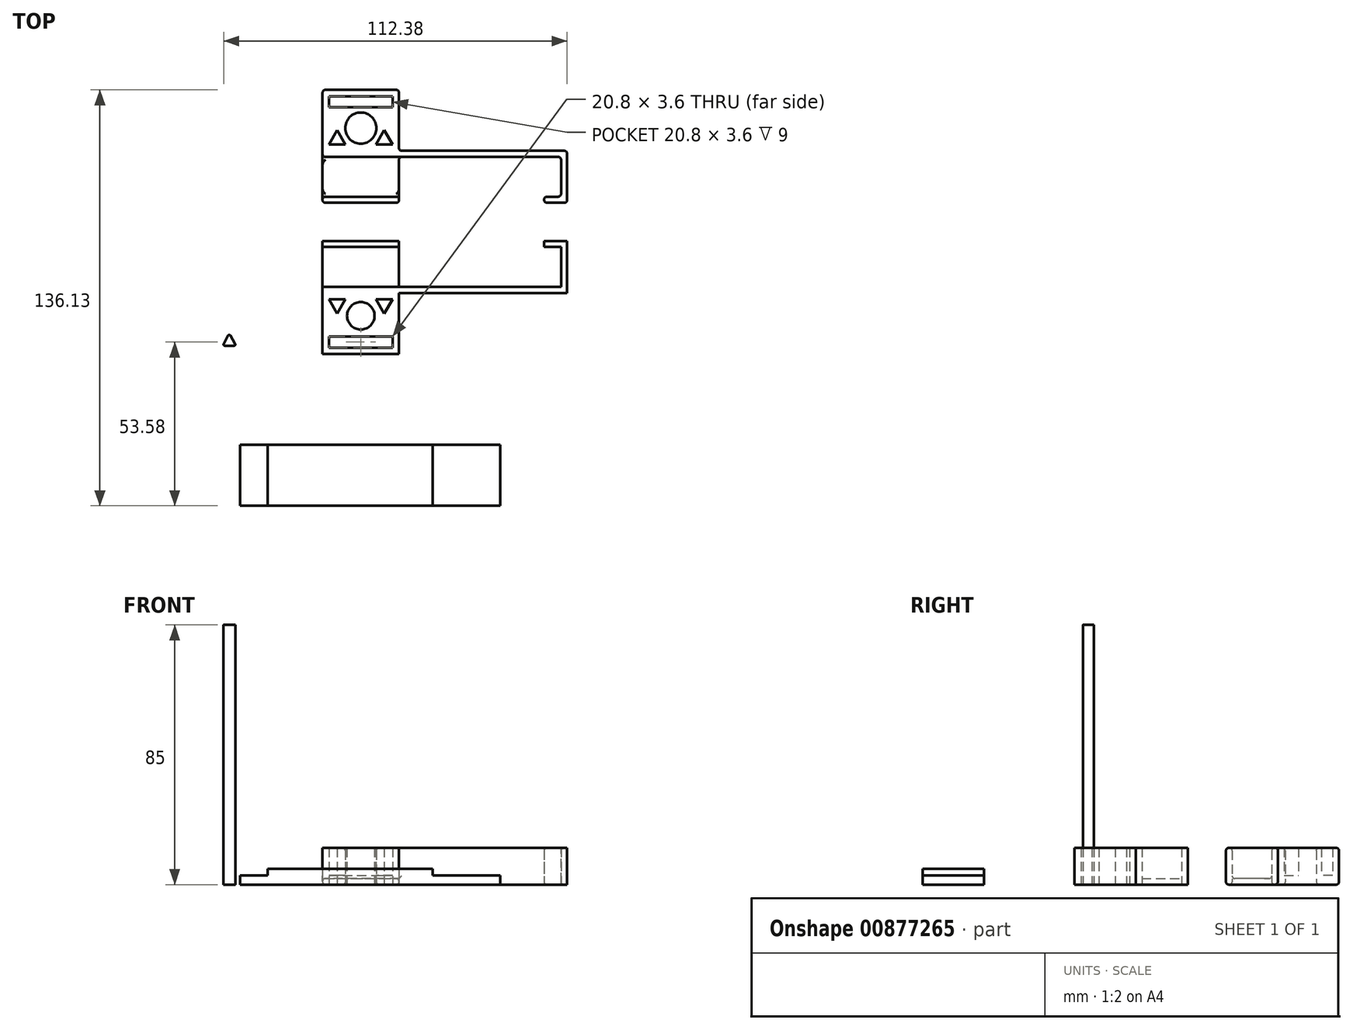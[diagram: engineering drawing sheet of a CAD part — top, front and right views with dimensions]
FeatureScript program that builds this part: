
annotation { "Feature Type Name" : "Feature", "Feature Type Description" : "" }
export const myFeature = defineFeature(function(context is Context, id is Id, definition is map)
    precondition{}
    {
        {
            var Q0;
            Q0=qCreatedBy(makeId("Top.planeOp"),FACE);
            var sketch = newSketch(context, id + "F0", { "sketchPlane" : qUnion([Q0])});
            skLineSegment(sketch, "E0.bottom", {"start": v(0, 0) * mm, "end": v(55, 0) * mm});
            skLineSegment(sketch, "E0.left", {"start": v(-25, 0) * mm, "end": v(-25, 2) * mm});
            skLineSegment(sketch, "E0.right", {"start": v(55, 0) * mm, "end": v(55, 2) * mm});
            skLineSegment(sketch, "E1.top", {"start": v(55, 17) * mm, "end": v(53, 17) * mm});
            skLineSegment(sketch, "E1.left", {"start": v(55, 2) * mm, "end": v(55, 17) * mm});
            skLineSegment(sketch, "E1.right", {"start": v(53, 2) * mm, "end": v(53, 15) * mm});
            skLineSegment(sketch, "E2.bottom", {"start": v(53, 17) * mm, "end": v(47.5, 17) * mm});
            skLineSegment(sketch, "E2.top", {"start": v(53, 15) * mm, "end": v(47.5, 15) * mm});
            skLineSegment(sketch, "E2.right", {"start": v(47.5, 17) * mm, "end": v(47.5, 15) * mm});
            skLineSegment(sketch, "E3", {"start": v(0, 2) * mm, "end": v(53, 2) * mm});
            skLineSegment(sketch, "E4.top", {"start": v(-25, -20) * mm, "end": v(0, -20) * mm});
            skLineSegment(sketch, "E4.left", {"start": v(-25, 0) * mm, "end": v(-25, -20) * mm});
            skLineSegment(sketch, "E4.right", {"start": v(0, 0) * mm, "end": v(0, -20) * mm});
            skLineSegment(sketch, "E5.top", {"start": v(-25, 17) * mm, "end": v(0, 17) * mm});
            skLineSegment(sketch, "E5.left", {"start": v(-25, 2) * mm, "end": v(-25, 17) * mm});
            skLineSegment(sketch, "E5.right", {"start": v(0, 2) * mm, "end": v(0, 17) * mm});
            skPoint(sketch, "E6", {"position": v(-12.5, -7.5) * mm});
            skCircle(sketch, "E7", {"center": v(-12.5, -7.5) * mm, "radius": 4.5 * mm});
            skLineSegment(sketch, "E8.bottom", {"start": v(0, 46.45) * mm, "end": v(-25, 46.45) * mm});
            skLineSegment(sketch, "E8.top", {"start": v(0, 66.45) * mm, "end": v(-25, 66.45) * mm});
            skLineSegment(sketch, "E8.left", {"start": v(0, 46.45) * mm, "end": v(0, 66.45) * mm});
            skLineSegment(sketch, "E8.right", {"start": v(-25, 46.45) * mm, "end": v(-25, 66.45) * mm});
            skLineSegment(sketch, "E9.bottom", {"start": v(0, 44.5) * mm, "end": v(-25, 44.5) * mm});
            skLineSegment(sketch, "E9.top", {"start": v(0, 29.5) * mm, "end": v(-25, 29.5) * mm});
            skLineSegment(sketch, "E9.left", {"start": v(0, 44.5) * mm, "end": v(0, 29.5) * mm});
            skLineSegment(sketch, "E9.right", {"start": v(-25, 44.5) * mm, "end": v(-25, 29.5) * mm});
            skPoint(sketch, "E10", {"position": v(-12.5, 53.95) * mm});
            skCircle(sketch, "E11", {"center": v(-12.5, 53.95) * mm, "radius": 5.1 * mm});
            skLineSegment(sketch, "E12", {"start": v(-25, 46.45) * mm, "end": v(-25, 44.5) * mm});
            skLineSegment(sketch, "E13", {"start": v(0, 46.5) * mm, "end": v(55, 46.5) * mm});
            skLineSegment(sketch, "E14", {"start": v(55, 46.5) * mm, "end": v(55, 29.5) * mm});
            skLineSegment(sketch, "E15", {"start": v(0, 44.5) * mm, "end": v(53, 44.5) * mm});
            skLineSegment(sketch, "E16", {"start": v(55, 29.5) * mm, "end": v(47.5, 29.5) * mm});
            skLineSegment(sketch, "E17", {"start": v(47.5, 29.5) * mm, "end": v(47.5, 31.5) * mm});
            skLineSegment(sketch, "E18", {"start": v(47.5, 31.5) * mm, "end": v(53, 31.5) * mm});
            skLineSegment(sketch, "E19", {"start": v(53, 31.5) * mm, "end": v(53, 44.5) * mm});
            skLineSegment(sketch, "E20", {"start": v(-25, 2) * mm, "end": v(0, 2) * mm});
            skLineSegment(sketch, "E21", {"start": v(0, 0) * mm, "end": v(-25, 0) * mm});
            skLineSegment(sketch, "E22", {"start": v(-20.2, 53.23) * mm, "end": v(-22.9, 48.55) * mm});
            skLineSegment(sketch, "E23", {"start": v(-22.9, 48.55) * mm, "end": v(-17.5, 48.55) * mm});
            skLineSegment(sketch, "E24", {"start": v(-17.5, 48.55) * mm, "end": v(-20.2, 53.23) * mm});
            skLineSegment(sketch, "E25", {"start": v(-12.5, 53.95) * mm, "end": v(-12.5, -32.35) * mm, "construction": true});
            skLineSegment(sketch, "E26.MirrorCS", {"start": v(-4.8, 53.23) * mm, "end": v(-2.1, 48.55) * mm});
            skLineSegment(sketch, "E27.MirrorCS", {"start": v(-7.5, 48.55) * mm, "end": v(-4.8, 53.23) * mm});
            skLineSegment(sketch, "E28.MirrorCS", {"start": v(-2.1, 48.55) * mm, "end": v(-7.5, 48.55) * mm});
            skLineSegment(sketch, "E29", {"start": v(-54.87, 23.25) * mm, "end": v(73.63, 23.25) * mm, "construction": true});
            skLineSegment(sketch, "E30.MirrorCS", {"start": v(-17.5, -2.05) * mm, "end": v(-20.2, -6.73) * mm});
            skLineSegment(sketch, "E31.MirrorCS", {"start": v(-20.2, -6.73) * mm, "end": v(-22.9, -2.05) * mm});
            skLineSegment(sketch, "E32.MirrorCS", {"start": v(-22.9, -2.05) * mm, "end": v(-17.5, -2.05) * mm});
            skLineSegment(sketch, "E33.MirrorCS", {"start": v(-2.1, -2.05) * mm, "end": v(-7.5, -2.05) * mm});
            skLineSegment(sketch, "E34.MirrorCS", {"start": v(-4.8, -6.73) * mm, "end": v(-2.1, -2.05) * mm});
            skLineSegment(sketch, "E35.MirrorCS", {"start": v(-7.5, -2.05) * mm, "end": v(-4.8, -6.73) * mm});
            skLineSegment(sketch, "E36.bottom", {"start": v(-22.9, -14.3) * mm, "end": v(-2.1, -14.3) * mm});
            skLineSegment(sketch, "E36.top", {"start": v(-22.9, -17.9) * mm, "end": v(-2.1, -17.9) * mm});
            skLineSegment(sketch, "E36.left", {"start": v(-22.9, -14.3) * mm, "end": v(-22.9, -17.9) * mm});
            skLineSegment(sketch, "E36.right", {"start": v(-2.1, -14.3) * mm, "end": v(-2.1, -17.9) * mm});
            skLineSegment(sketch, "E37.bottom", {"start": v(-22.9, 64.35) * mm, "end": v(-2.1, 64.35) * mm});
            skLineSegment(sketch, "E37.top", {"start": v(-22.9, 60.75) * mm, "end": v(-2.1, 60.75) * mm});
            skLineSegment(sketch, "E37.left", {"start": v(-22.9, 64.35) * mm, "end": v(-22.9, 60.75) * mm});
            skLineSegment(sketch, "E37.right", {"start": v(-2.1, 64.35) * mm, "end": v(-2.1, 60.75) * mm});
            skSolve(sketch);
        }
        {
            var Q0;
            Q0=makeQuery(id+"F0.imprint","IMPRINT",FACE,{"disambiguationData":[TD([[makeQuery(id+"F0.imprint","IMPRINT",EDGE,{"derivedFrom":sQuery(id+"F0.wireOp",EDGE,"E5.top")}),-1.0]])]});
            var Q1;
            Q1=makeQuery(id+"F0.imprint","IMPRINT",FACE,{"disambiguationData":[TD([[makeQuery(id+"F0.imprint","IMPRINT",EDGE,{"derivedFrom":sQuery(id+"F0.wireOp",EDGE,"E9.bottom")}),1.0]])]});
            extrude(context, id + "F1", {"entities" : qUnion([Q0, Q1]), "depth" : 2 * mm, "offsetDistance" : 25 * mm});
        }
        {
            var Q0;
            Q0=makeQuery(id+"F0.imprint","IMPRINT",FACE,{"disambiguationData":[TD([[makeQuery(id+"F0.imprint","IMPRINT",EDGE,{"derivedFrom":sQuery(id+"F0.wireOp",EDGE,"E0.bottom")}),1.0]])]});
            var Q1;
            Q1=makeQuery(id+"F0.imprint","IMPRINT",FACE,{"disambiguationData":[TD([[makeQuery(id+"F0.imprint","IMPRINT",EDGE,{"derivedFrom":sQuery(id+"F0.wireOp",EDGE,"E4.top")}),1.0]])]});
            var Q2;
            Q2=makeQuery(id+"F0.imprint","IMPRINT",FACE,{"disambiguationData":[TD([[makeQuery(id+"F0.imprint","IMPRINT",EDGE,{"derivedFrom":sQuery(id+"F0.wireOp",EDGE,"E22")}),1.0]])]});
            var Q3;
            Q3=makeQuery(id+"F0.imprint","IMPRINT",FACE,{"disambiguationData":[TD([[makeQuery(id+"F0.imprint","IMPRINT",EDGE,{"derivedFrom":sQuery(id+"F0.wireOp",EDGE,"E26.MirrorCS")}),-1.0]])]});
            var Q4;
            {var subQ0=sQuery(id+"F0.wireOp",EDGE,"E8.bottom");Q4=makeQuery(id+"F0.imprint","IMPRINT",FACE,{"disambiguationData":[TD([[makeQuery(id+"F0.imprint","IMPRINT",EDGE,{"derivedFrom":subQ0}),-1.0]])]});}
            var Q5;
            {var subQ0=sQuery(id+"F0.wireOp",EDGE,"E8.bottom");Q5=makeQuery(id+"F0.imprint","IMPRINT",FACE,{"disambiguationData":[TD([[makeQuery(id+"F0.imprint","IMPRINT",EDGE,{"derivedFrom":subQ0}),-1.0]])]});}
            var Q6;
            Q6=makeQuery(id+"F0.imprint","IMPRINT",FACE,{"disambiguationData":[TD([[makeQuery(id+"F0.imprint","IMPRINT",EDGE,{"derivedFrom":sQuery(id+"F0.wireOp",EDGE,"E37.bottom")}),-1.0]])]});
            var Q7;
            {var subQ0=sQuery(id+"F0.wireOp",EDGE,"E8.bottom");Q7=makeQuery(id+"F0.imprint","IMPRINT",FACE,{"disambiguationData":[TD([[makeQuery(id+"F0.imprint","IMPRINT",EDGE,{"derivedFrom":subQ0}),-1.0]])]});}
            var Q8;
            {var subQ1=sQuery(id+"F0.wireOp",EDGE,"E8.bottom");Q8=makeQuery(id+"F0.imprint","IMPRINT",FACE,{"disambiguationData":[TD([[makeQuery(id+"F0.imprint","IMPRINT",EDGE,{"derivedFrom":subQ1}),1.0]])]});}
            extrude(context, id + "F2", {"entities" : qUnion([Q0, Q1, Q2, Q3, Q4, Q5, Q6, Q7, Q8]), "depth" : 12 * mm, "offsetDistance" : 25 * mm});
        }
        {
            var Q0;
            Q0=makeQuery(id+"F1.opExtrude","CAP_FACE",FACE,{"disambiguationData":[OSD([sQuery(id+"F0.wireOp",EDGE,"E5.bottom"),sQuery(id+"F0.wireOp",EDGE,"E5.top"),sQuery(id+"F0.wireOp",EDGE,"E5.left"),sQuery(id+"F0.wireOp",EDGE,"E5.right")])],"isStart":false});
            var sketch = newSketch(context, id + "F3", { "sketchPlane" : qUnion([Q0])});
            skLineSegment(sketch, "E38.bottom", {"start": v(-25, 17) * mm, "end": v(0, 17) * mm});
            skLineSegment(sketch, "E38.top", {"start": v(-25, 15) * mm, "end": v(0, 15) * mm});
            skLineSegment(sketch, "E38.left", {"start": v(-25, 17) * mm, "end": v(-25, 15) * mm});
            skLineSegment(sketch, "E38.right", {"start": v(0, 17) * mm, "end": v(0, 15) * mm});
            skLineSegment(sketch, "E39.bottom", {"start": v(-25, 31.5) * mm, "end": v(0, 31.5) * mm});
            skLineSegment(sketch, "E39.top", {"start": v(-25, 29.5) * mm, "end": v(0, 29.5) * mm});
            skLineSegment(sketch, "E39.left", {"start": v(-25, 31.5) * mm, "end": v(-25, 29.5) * mm});
            skLineSegment(sketch, "E39.right", {"start": v(0, 31.5) * mm, "end": v(0, 29.5) * mm});
            skSolve(sketch);
        }
        {
            var Q0;
            Q0=makeQuery(id+"F3.imprint","IMPRINT",FACE,{"disambiguationData":[TD([[makeQuery(id+"F3.imprint","IMPRINT",EDGE,{"derivedFrom":sQuery(id+"F3.wireOp",EDGE,"E38.bottom")}),-1.0]])]});
            var Q1;
            Q1=makeQuery(id+"F3.imprint","IMPRINT",FACE,{"disambiguationData":[TD([[makeQuery(id+"F3.imprint","IMPRINT",EDGE,{"derivedFrom":sQuery(id+"F3.wireOp",EDGE,"E39.bottom")}),-1.0]])]});
            extrude(context, id + "F4", {"entities" : qUnion([Q0, Q1]), "depth" : 10 * mm, "offsetDistance" : 25 * mm});
        }
        {
            var Q0;
            Q0=makeQuery(id+"F1.opExtrude","SWEPT_BODY",BODY,{"disambiguationData":[OSD([sQuery(id+"F0.wireOp",EDGE,"E5.top"),sQuery(id+"F0.wireOp",EDGE,"E5.left"),sQuery(id+"F0.wireOp",EDGE,"E5.right"),sQuery(id+"F0.wireOp",EDGE,"E20")])]});
            var Q1;
            Q1=makeQuery(id+"F4.opExtrude","SWEPT_BODY",BODY,{"disambiguationData":[OSD([sQuery(id+"F3.wireOp",EDGE,"E38.bottom"),sQuery(id+"F3.wireOp",EDGE,"E38.top"),sQuery(id+"F3.wireOp",EDGE,"E38.left"),sQuery(id+"F3.wireOp",EDGE,"E38.right")])]});
            var Q2;
            Q2=makeQuery(id+"F2.opExtrude","SWEPT_BODY",BODY,{"disambiguationData":[OSD([sQuery(id+"F0.wireOp",EDGE,"E0.bottom"),sQuery(id+"F0.wireOp",EDGE,"E0.left"),sQuery(id+"F0.wireOp",EDGE,"E0.right"),sQuery(id+"F0.wireOp",EDGE,"E1.top"),sQuery(id+"F0.wireOp",EDGE,"E1.left"),sQuery(id+"F0.wireOp",EDGE,"E1.right"),sQuery(id+"F0.wireOp",EDGE,"E2.bottom"),sQuery(id+"F0.wireOp",EDGE,"E2.top"),sQuery(id+"F0.wireOp",EDGE,"E2.right"),sQuery(id+"F0.wireOp",EDGE,"E3"),sQuery(id+"F0.wireOp",EDGE,"E4.top"),sQuery(id+"F0.wireOp",EDGE,"E4.left"),sQuery(id+"F0.wireOp",EDGE,"E4.right"),sQuery(id+"F0.wireOp",EDGE,"E7"),sQuery(id+"F0.wireOp",EDGE,"E20")])]});
            booleanBodies(context, id + "F5", {"operationType" : BooleanOperationType.UNION, "tools" : qUnion([Q0, Q1, Q2])});
        }
        {
            var Q0;
            Q0=makeQuery(id+"F1.opExtrude","SWEPT_BODY",BODY,{"disambiguationData":[OSD([sQuery(id+"F0.wireOp",EDGE,"E9.bottom"),sQuery(id+"F0.wireOp",EDGE,"E9.top"),sQuery(id+"F0.wireOp",EDGE,"E9.left"),sQuery(id+"F0.wireOp",EDGE,"E9.right")])]});
            var Q1;
            Q1=makeQuery(id+"F2.opExtrude","SWEPT_BODY",BODY,{"disambiguationData":[OSD([sQuery(id+"F0.wireOp",EDGE,"E8.top"),sQuery(id+"F0.wireOp",EDGE,"E8.left"),sQuery(id+"F0.wireOp",EDGE,"E8.right"),sQuery(id+"F0.wireOp",EDGE,"E9.bottom"),sQuery(id+"F0.wireOp",EDGE,"E11"),sQuery(id+"F0.wireOp",EDGE,"E12"),sQuery(id+"F0.wireOp",EDGE,"E13"),sQuery(id+"F0.wireOp",EDGE,"E14"),sQuery(id+"F0.wireOp",EDGE,"E15"),sQuery(id+"F0.wireOp",EDGE,"E16"),sQuery(id+"F0.wireOp",EDGE,"E17"),sQuery(id+"F0.wireOp",EDGE,"E18"),sQuery(id+"F0.wireOp",EDGE,"E19")])]});
            var Q2;
            Q2=makeQuery(id+"F4.opExtrude","SWEPT_BODY",BODY,{"disambiguationData":[OSD([sQuery(id+"F3.wireOp",EDGE,"E39.bottom"),sQuery(id+"F3.wireOp",EDGE,"E39.top"),sQuery(id+"F3.wireOp",EDGE,"E39.left"),sQuery(id+"F3.wireOp",EDGE,"E39.right")])]});
            booleanBodies(context, id + "F6", {"operationType" : BooleanOperationType.UNION, "tools" : qUnion([Q0, Q1, Q2])});
        }
        {
            var Q0;
            Q0=makeQuery(id+"F2.opExtrude","SWEPT_FACE",FACE,{"disambiguationData":[OSD([sQuery(id+"F0.wireOp",EDGE,"E19")])]});
            var Q1;
            Q1=makeQuery(id+"F2.opExtrude","SWEPT_FACE",FACE,{"disambiguationData":[OSD([sQuery(id+"F0.wireOp",EDGE,"E17")])]});
            var Q2;
            Q2=makeQuery(id+"F2.opExtrude","CAP_FACE",FACE,{"disambiguationData":[OSD([sQuery(id+"F0.wireOp",EDGE,"E8.top"),sQuery(id+"F0.wireOp",EDGE,"E8.left"),sQuery(id+"F0.wireOp",EDGE,"E8.right"),sQuery(id+"F0.wireOp",EDGE,"E9.bottom"),sQuery(id+"F0.wireOp",EDGE,"E11"),sQuery(id+"F0.wireOp",EDGE,"E12"),sQuery(id+"F0.wireOp",EDGE,"E13"),sQuery(id+"F0.wireOp",EDGE,"E14"),sQuery(id+"F0.wireOp",EDGE,"E15"),sQuery(id+"F0.wireOp",EDGE,"E16"),sQuery(id+"F0.wireOp",EDGE,"E17"),sQuery(id+"F0.wireOp",EDGE,"E18"),sQuery(id+"F0.wireOp",EDGE,"E19")])],"isStart":false});
            var Q3;
            {var subQ0=sQuery(id+"F0.wireOp",EDGE,"E9.bottom");Q3=makeQuery(id+"F6.opBoolean","MERGE",FACE,{"derivedFrom":[makeQuery(id+"F1.opExtrude","CAP_FACE",FACE,{"disambiguationData":[OSD([subQ0,sQuery(id+"F0.wireOp",EDGE,"E9.top"),sQuery(id+"F0.wireOp",EDGE,"E9.left"),sQuery(id+"F0.wireOp",EDGE,"E9.right")])],"isStart":true}),makeQuery(id+"F2.opExtrude","CAP_FACE",FACE,{"disambiguationData":[OSD([sQuery(id+"F0.wireOp",EDGE,"E8.top"),sQuery(id+"F0.wireOp",EDGE,"E8.left"),sQuery(id+"F0.wireOp",EDGE,"E8.right"),subQ0,sQuery(id+"F0.wireOp",EDGE,"E11"),sQuery(id+"F0.wireOp",EDGE,"E12"),sQuery(id+"F0.wireOp",EDGE,"E13"),sQuery(id+"F0.wireOp",EDGE,"E14"),sQuery(id+"F0.wireOp",EDGE,"E15"),sQuery(id+"F0.wireOp",EDGE,"E16"),sQuery(id+"F0.wireOp",EDGE,"E17"),sQuery(id+"F0.wireOp",EDGE,"E18"),sQuery(id+"F0.wireOp",EDGE,"E19")])],"isStart":true})]});}
            var Q4;
            Q4=makeQuery(id+"F2.opExtrude","SWEPT_FACE",FACE,{"disambiguationData":[OSD([sQuery(id+"F0.wireOp",EDGE,"E14")])]});
            var Q5;
            Q5=makeQuery(id+"F2.opExtrude","SWEPT_FACE",FACE,{"disambiguationData":[OSD([sQuery(id+"F0.wireOp",EDGE,"E1.top"),sQuery(id+"F0.wireOp",EDGE,"E2.bottom")])]});
            var Q6;
            Q6=makeQuery(id+"F2.opExtrude","SWEPT_FACE",FACE,{"disambiguationData":[OSD([sQuery(id+"F0.wireOp",EDGE,"E0.right"),sQuery(id+"F0.wireOp",EDGE,"E1.left")])]});
            var Q7;
            Q7=makeQuery(id+"F2.opExtrude","SWEPT_FACE",FACE,{"disambiguationData":[OSD([sQuery(id+"F0.wireOp",EDGE,"E1.right")])]});
            var Q8;
            Q8=makeQuery(id+"F2.opExtrude","SWEPT_FACE",FACE,{"disambiguationData":[OSD([sQuery(id+"F0.wireOp",EDGE,"E2.top")])]});
            var Q9;
            Q9=makeQuery(id+"F2.opExtrude","SWEPT_FACE",FACE,{"disambiguationData":[OSD([sQuery(id+"F0.wireOp",EDGE,"E8.top")])]});
            var Q10;
            Q10=makeQuery(id+"F2.opExtrude","SWEPT_FACE",FACE,{"disambiguationData":[OSD([sQuery(id+"F0.wireOp",EDGE,"E9.bottom"),sQuery(id+"F0.wireOp",EDGE,"E15")])]});
            var Q11;
            Q11=makeQuery(id+"F6.opBoolean","MERGE",FACE,{"derivedFrom":[makeQuery(id+"F1.opExtrude","SWEPT_FACE",FACE,{"disambiguationData":[OSD([sQuery(id+"F0.wireOp",EDGE,"E9.top")])]}),makeQuery(id+"F4.opExtrude","SWEPT_FACE",FACE,{"disambiguationData":[OSD([sQuery(id+"F3.wireOp",EDGE,"E39.top")])]})]});
            var Q12;
            Q12=makeQuery(id+"F4.opExtrude","CAP_FACE",FACE,{"disambiguationData":[OSD([sQuery(id+"F3.wireOp",EDGE,"E39.bottom"),sQuery(id+"F3.wireOp",EDGE,"E39.top"),sQuery(id+"F3.wireOp",EDGE,"E39.left"),sQuery(id+"F3.wireOp",EDGE,"E39.right")])],"isStart":false});
            var Q13;
            Q13=makeQuery(id+"F2.opExtrude","SWEPT_FACE",FACE,{"disambiguationData":[OSD([sQuery(id+"F0.wireOp",EDGE,"E8.left")])]});
            var Q14;
            Q14=makeQuery(id+"F4.opExtrude","CAP_EDGE",EDGE,{"disambiguationData":[OSD([sQuery(id+"F3.wireOp",EDGE,"E39.bottom")])],"isStart":true});
            var Q15;
            Q15=makeQuery(id+"F2.opExtrude","SWEPT_FACE",FACE,{"disambiguationData":[OSD([sQuery(id+"F0.wireOp",EDGE,"E0.bottom")])]});
            var Q16;
            Q16=makeQuery(id+"F5.opBoolean","MERGE",FACE,{"derivedFrom":[makeQuery(id+"F1.opExtrude","SWEPT_FACE",FACE,{"disambiguationData":[OSD([sQuery(id+"F0.wireOp",EDGE,"E5.top")])]}),makeQuery(id+"F4.opExtrude","SWEPT_FACE",FACE,{"disambiguationData":[OSD([sQuery(id+"F3.wireOp",EDGE,"E38.bottom")])]})]});
            var Q17;
            Q17=makeQuery(id+"F1.opExtrude","CAP_FACE",FACE,{"disambiguationData":[OSD([sQuery(id+"F0.wireOp",EDGE,"E5.top"),sQuery(id+"F0.wireOp",EDGE,"E5.left"),sQuery(id+"F0.wireOp",EDGE,"E5.right"),sQuery(id+"F0.wireOp",EDGE,"E20")])],"isStart":false});
            var Q18;
            Q18=makeQuery(id+"F4.opExtrude","CAP_EDGE",EDGE,{"disambiguationData":[OSD([sQuery(id+"F3.wireOp",EDGE,"E38.left")])],"isStart":false});
            var Q19;
            Q19=makeQuery(id+"F4.opExtrude","CAP_EDGE",EDGE,{"disambiguationData":[OSD([sQuery(id+"F3.wireOp",EDGE,"E38.right")])],"isStart":false});
            var Q20;
            Q20=makeQuery(id+"F4.opExtrude","CAP_EDGE",EDGE,{"disambiguationData":[OSD([sQuery(id+"F3.wireOp",EDGE,"E38.top")])],"isStart":false});
            var Q21;
            Q21=makeQuery(id+"F5.opBoolean","MERGE",EDGE,{"derivedFrom":[makeQuery(id+"F1.opExtrude","CAP_EDGE",EDGE,{"disambiguationData":[OSD([sQuery(id+"F0.wireOp",EDGE,"E5.left")])],"isStart":true}),makeQuery(id+"F2.opExtrude","CAP_EDGE",EDGE,{"disambiguationData":[OSD([sQuery(id+"F0.wireOp",EDGE,"E0.left"),sQuery(id+"F0.wireOp",EDGE,"E4.left")])],"isStart":true})]});
            var Q22;
            Q22=makeQuery(id+"F2.opExtrude","SWEPT_FACE",FACE,{"disambiguationData":[OSD([sQuery(id+"F0.wireOp",EDGE,"E4.top")])]});
            var Q23;
            Q23=makeQuery(id+"F2.opExtrude","CAP_EDGE",EDGE,{"disambiguationData":[OSD([sQuery(id+"F0.wireOp",EDGE,"E0.left"),sQuery(id+"F0.wireOp",EDGE,"E4.left")])],"isStart":false});
            var Q24;
            Q24=makeQuery(id+"F4.opExtrude","SWEPT_FACE",FACE,{"disambiguationData":[OSD([sQuery(id+"F3.wireOp",EDGE,"E39.bottom")])]});
            var Q25;
            Q25=makeQuery(id+"F2.opExtrude","CAP_EDGE",EDGE,{"disambiguationData":[OSD([sQuery(id+"F0.wireOp",EDGE,"E2.right")])],"isStart":false});
            var Q26;
            Q26=makeQuery(id+"F2.opExtrude","CAP_EDGE",EDGE,{"disambiguationData":[OSD([sQuery(id+"F0.wireOp",EDGE,"E2.right")])],"isStart":true});
            fillet(context, id + "F7", {"entities" : qUnion([Q0, Q1, Q2, Q3, Q4, Q5, Q6, Q7, Q8, Q9, Q10, Q11, Q12, Q13, Q14, Q15, Q16, Q17, Q18, Q19, Q20, Q21, Q22, Q23, Q24, Q25, Q26]), "radius" : .9 * mm, "tangentPropagation" : true, "allowEdgeOverflow" : false});
        }
        {
            var Q0;
            Q0=qCreatedBy(makeId("Top.planeOp"),FACE);
            cPlane(context, id + "F8", {"entities" : qUnion([Q0]), "cplaneType" : CPlaneType.OFFSET, "offset" : 3 * mm, "width" : 150 * mm, "height" : 150 * mm});
        }
        {
            var Q0;
            Q0=qCreatedBy(id+"F8.planeOp",FACE);
            var sketch = newSketch(context, id + "F9", { "sketchPlane" : qUnion([Q0])});
            skLineSegment(sketch, "E40.0", {"start": v(-20.2, 53.23) * mm, "end": v(-22.9, 48.55) * mm});
            skLineSegment(sketch, "E41.0", {"start": v(-22.9, 48.55) * mm, "end": v(-17.5, 48.55) * mm});
            skLineSegment(sketch, "E42.0", {"start": v(-17.5, 48.55) * mm, "end": v(-20.2, 53.23) * mm});
            skLineSegment(sketch, "E43.0", {"start": v(-7.5, 48.55) * mm, "end": v(-4.8, 53.23) * mm});
            skLineSegment(sketch, "E44.0", {"start": v(-4.8, 53.23) * mm, "end": v(-2.1, 48.55) * mm});
            skLineSegment(sketch, "E45.0", {"start": v(-2.1, 48.55) * mm, "end": v(-7.5, 48.55) * mm});
            skLineSegment(sketch, "E46.0", {"start": v(-22.9, 64.35) * mm, "end": v(-2.1, 64.35) * mm});
            skLineSegment(sketch, "E47.0", {"start": v(-22.9, 60.75) * mm, "end": v(-2.1, 60.75) * mm});
            skLineSegment(sketch, "E48.0", {"start": v(-22.9, 64.35) * mm, "end": v(-22.9, 60.75) * mm});
            skLineSegment(sketch, "E49.0", {"start": v(-2.1, 64.35) * mm, "end": v(-2.1, 60.75) * mm});
            skSolve(sketch);
        }
        {
            var Q0;
            Q0=qSketchRegion(id+"F9",true);
            var Q1;
            Q1=makeQuery(id+"F2.opExtrude","CAP_FACE",FACE,{"disambiguationData":[OSD([sQuery(id+"F0.wireOp",EDGE,"E8.top"),sQuery(id+"F0.wireOp",EDGE,"E8.left"),sQuery(id+"F0.wireOp",EDGE,"E8.right"),sQuery(id+"F0.wireOp",EDGE,"E9.bottom"),sQuery(id+"F0.wireOp",EDGE,"E11"),sQuery(id+"F0.wireOp",EDGE,"E12"),sQuery(id+"F0.wireOp",EDGE,"E13"),sQuery(id+"F0.wireOp",EDGE,"E14"),sQuery(id+"F0.wireOp",EDGE,"E15"),sQuery(id+"F0.wireOp",EDGE,"E16"),sQuery(id+"F0.wireOp",EDGE,"E17"),sQuery(id+"F0.wireOp",EDGE,"E18"),sQuery(id+"F0.wireOp",EDGE,"E19")])],"isStart":false});
            extrude(context, id + "F10", {"entities" : qUnion([Q0]), "operationType" : NewBodyOperationType.REMOVE, "endBound" : BoundingType.UP_TO_SURFACE, "depth" : 25 * mm, "endBoundEntityFace" : qUnion([Q1]), "offsetDistance" : 25 * mm});
        }
        {
            var Q0;
            Q0=qCreatedBy(makeId("Top.planeOp"),FACE);
            var sketch = newSketch(context, id + "F11", { "sketchPlane" : qUnion([Q0])});
            skLineSegment(sketch, "E50", {"start": v(-55.89, -13.94) * mm, "end": v(-57.34, -16.7) * mm});
            skLineSegment(sketch, "E51", {"start": v(-56.98, -17.29) * mm, "end": v(-53.94, -17.29) * mm});
            skLineSegment(sketch, "E52", {"start": v(-53.6, -16.69) * mm, "end": v(-55.19, -13.93) * mm});
            skPoint(sketch, "E53.visualSharp", {"position": v(-55.55, -13.3) * mm});
            skArc(sketch, "E53.filletArc", {"start": v(-55.19, -13.93) * mm, "mid": v(-55.54, -13.73) * mm, "end": v(-55.89, -13.94) * mm});
            skPoint(sketch, "E54.visualSharp", {"position": v(-57.65, -17.29) * mm});
            skArc(sketch, "E54.filletArc", {"start": v(-57.34, -16.7) * mm, "mid": v(-57.33, -17.1) * mm, "end": v(-56.98, -17.29) * mm});
            skPoint(sketch, "E55.visualSharp", {"position": v(-53.25, -17.29) * mm});
            skArc(sketch, "E55.filletArc", {"start": v(-53.94, -17.29) * mm, "mid": v(-53.6, -17.09) * mm, "end": v(-53.6, -16.69) * mm});
            skSolve(sketch);
        }
        {
            var Q0;
            Q0=makeQuery(id+"F11.imprint","IMPRINT",FACE,{"disambiguationData":[TD([[makeQuery(id+"F11.imprint","IMPRINT",EDGE,{"derivedFrom":sQuery(id+"F11.wireOp",EDGE,"E50")}),1.0]])]});
            extrude(context, id + "F12", {"entities" : qUnion([Q0]), "depth" : 85 * mm, "offsetDistance" : 25 * mm});
        }
        {
            var Q0;
            Q0=qCreatedBy(makeId("Top.planeOp"),FACE);
            var sketch = newSketch(context, id + "F13", { "sketchPlane" : qUnion([Q0])});
            skLineSegment(sketch, "E56.bottom", {"start": v(-51.95, -49.68) * mm, "end": v(33.05, -49.68) * mm});
            skLineSegment(sketch, "E56.top", {"start": v(-51.95, -69.68) * mm, "end": v(33.05, -69.68) * mm});
            skLineSegment(sketch, "E56.left", {"start": v(-51.95, -49.68) * mm, "end": v(-51.95, -69.68) * mm});
            skLineSegment(sketch, "E56.right", {"start": v(33.05, -49.68) * mm, "end": v(33.05, -69.68) * mm});
            skSolve(sketch);
        }
        {
            var Q0;
            Q0=makeQuery(id+"F13.imprint","IMPRINT",FACE,{"disambiguationData":[TD([[makeQuery(id+"F13.imprint","IMPRINT",EDGE,{"derivedFrom":sQuery(id+"F13.wireOp",EDGE,"E56.bottom")}),-1.0]])]});
            extrude(context, id + "F14", {"entities" : qUnion([Q0]), "depth" : 3 * mm, "offsetDistance" : 25 * mm});
        }
        {
            var Q0;
            Q0=makeQuery(id+"F14.opExtrude","CAP_FACE",FACE,{"disambiguationData":[OSD([sQuery(id+"F13.wireOp",EDGE,"E56.bottom"),sQuery(id+"F13.wireOp",EDGE,"E56.top"),sQuery(id+"F13.wireOp",EDGE,"E56.left"),sQuery(id+"F13.wireOp",EDGE,"E56.right")])],"isStart":false});
            var sketch = newSketch(context, id + "F15", { "sketchPlane" : qUnion([Q0])});
            skLineSegment(sketch, "E57.bottom", {"start": v(-42.95, -49.68) * mm, "end": v(11.05, -49.68) * mm});
            skLineSegment(sketch, "E57.top", {"start": v(-42.95, -69.68) * mm, "end": v(11.05, -69.68) * mm});
            skLineSegment(sketch, "E57.left", {"start": v(-42.95, -49.68) * mm, "end": v(-42.95, -69.68) * mm});
            skLineSegment(sketch, "E57.right", {"start": v(11.05, -49.68) * mm, "end": v(11.05, -69.68) * mm});
            skSolve(sketch);
        }
        {
            var Q0;
            Q0=makeQuery(id+"F15.imprint","IMPRINT",FACE,{"disambiguationData":[TD([[makeQuery(id+"F15.imprint","IMPRINT",EDGE,{"derivedFrom":sQuery(id+"F15.wireOp",EDGE,"E57.bottom")}),-1.0]])]});
            extrude(context, id + "F16", {"entities" : qUnion([Q0]), "operationType" : NewBodyOperationType.ADD, "depth" : 2.1 * mm, "offsetDistance" : 25 * mm});
        }
    });
